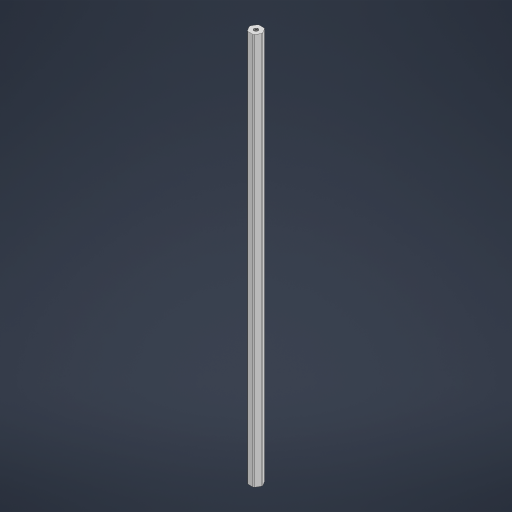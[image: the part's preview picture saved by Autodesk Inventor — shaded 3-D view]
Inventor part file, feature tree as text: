
AUTODESK INVENTOR PART (.ipt)
format: ipt  version: 2023 (Build 270158000, 158)  size: 754,688 bytes
history: native  units: in
note: dims shown in document units (in); Inventor stores cm internally (conversion verified against a paired STEP export)
features: mirror x1
ambient origin geometry x8: Origin, YZ Plane, XZ Plane, XY Plane, X Axis, Y Axis, Z Axis, Center Point
bodies: Solid1 (feature_tree)
feature tree (1):
  mirror  "Mirror2"
